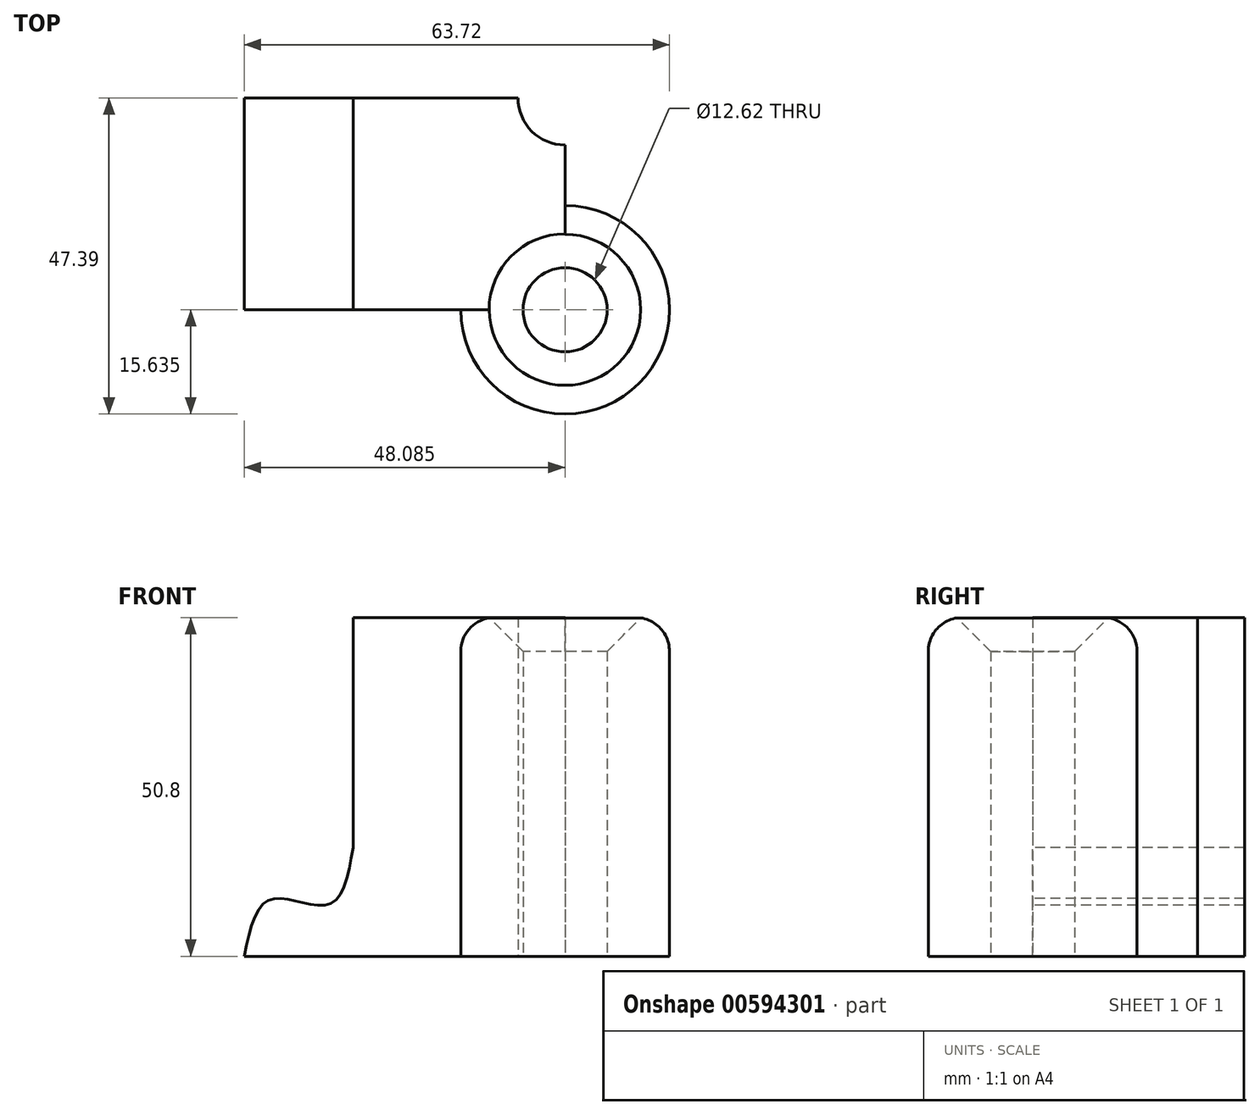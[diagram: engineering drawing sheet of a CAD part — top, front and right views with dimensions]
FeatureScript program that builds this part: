
annotation { "Feature Type Name" : "Feature", "Feature Type Description" : "" }
export const myFeature = defineFeature(function(context is Context, id is Id, definition is map)
    precondition{}
    {
        {
            var Q0;
            Q0=qCreatedBy(makeId("Top.planeOp"),FACE);
            var sketch = newSketch(context, id + "F0", { "sketchPlane" : qUnion([Q0])});
            skLineSegment(sketch, "E0.bottom", {"start": v(8.83, 15.88) * mm, "end": v(-15.88, 15.88) * mm});
            skLineSegment(sketch, "E0.top", {"start": v(0.24, -15.88) * mm, "end": v(-15.87, -15.88) * mm});
            skLineSegment(sketch, "E0.left", {"start": v(15.88, 8.83) * mm, "end": v(15.88, -0.24) * mm});
            skLineSegment(sketch, "E0.right", {"start": v(-15.88, 15.88) * mm, "end": v(-15.87, -15.88) * mm});
            skPoint(sketch, "E0.middle", {"position": v(0, 0) * mm});
            skArc(sketch, "E1", {"start": v(8.83, 15.88) * mm, "mid": v(10.89, 10.89) * mm, "end": v(15.88, 8.83) * mm});
            skArc(sketch, "E2", {"start": v(0.24, -15.87) * mm, "mid": v(26.93, -26.93) * mm, "end": v(15.87, -0.24) * mm});
            skCircle(sketch, "E3", {"center": v(15.88, -15.88) * mm, "radius": 6.3 * mm});
            skSolve(sketch);
        }
        {
            var Q0;
            Q0 = qSketchRegion(id + "F0", true);
            extrude(context, id + "F1", {"entities" : qUnion([Q0]), "depth" : 50.8 * mm, "offsetDistance" : 25.4 * mm});
        }
        {
            var Q0;
            Q0=makeQuery(id+"F1.opExtrude","SWEPT_FACE",FACE,{"disambiguationData":[OSD([sQuery(id+"F0.wireOp",EDGE,"E0.top")])]});
            var sketch = newSketch(context, id + "F2", { "sketchPlane" : qUnion([Q0])});
            skPoint(sketch, "E4.1.internal.snap0", {"position": v(-24.04, 0) * mm});
            skPoint(sketch, "E5.3.internal.snap0", {"position": v(-15.87, 8.16) * mm});
            skFitSpline(sketch, "E5", {"points": [v(-32.2, 0) * mm, v(-29, 8.16) * mm, v(-24.04, 8.16) * mm, v(-18.8, 8.16) * mm, v(-15.88, 16.32) * mm], "startDerivative": vector(7.96, 36.9) * mm, "endDerivative": vector(6.47, 37.03) * mm});
            skLineSegment(sketch, "E6", {"start": v(-32.2, 0) * mm, "end": v(-15.87, 0) * mm});
            skLineSegment(sketch, "E7", {"start": v(-15.87, 0) * mm, "end": v(-15.88, 16.32) * mm});
            skSolve(sketch);
        }
        {
            var Q0;
            Q0 = qSketchRegion(id + "F2", true);
            extrude(context, id + "F3", {"entities" : qUnion([Q0]), "operationType" : NewBodyOperationType.ADD, "oppositeDirection" : true, "depth" : 31.75 * mm, "offsetDistance" : 25.4 * mm});
        }
        {
            var Q0;
            Q0=makeQuery(id+"F1.opExtrude","CAP_EDGE",EDGE,{"disambiguationData":[OSD([sQuery(id+"F0.wireOp",EDGE,"E3")])],"isStart":false});
            chamfer(context, id + "F4", {"entities" : qUnion([Q0]), "width" : 5.08 * mm, "tangentPropagation" : true});
        }
        {
            var Q0;
            Q0=makeQuery(id+"F1.opExtrude","CAP_EDGE",EDGE,{"disambiguationData":[OSD([sQuery(id+"F0.wireOp",EDGE,"E2")])],"isStart":false});
            fillet(context, id + "F5", {"entities" : qUnion([Q0]), "radius" : 5.08 * mm, "tangentPropagation" : true, "allowEdgeOverflow" : false});
        }
    });
